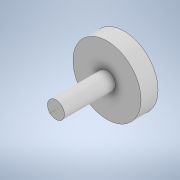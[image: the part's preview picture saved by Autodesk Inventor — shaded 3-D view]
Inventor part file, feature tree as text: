
AUTODESK INVENTOR PART (.ipt)
format: ipt  version: 2021.1 (Build 251245000, 245)  size: 105,984 bytes
history: native  units: in
note: dims shown in document units (in); Inventor stores cm internally (conversion verified against a paired STEP export)
features: extrude x3, sketch x3
ambient origin geometry x8: Origin, YZ Plane, XZ Plane, XY Plane, X Axis, Y Axis, Z Axis, Center Point
bodies: Solid1 (feature_tree)
feature tree (6):
  extrude  "Extrusion1"  Depth=0.25in TaperAngle=0.0deg
  extrude  "Extrusion2"  Depth=0.25in TaperAngle=0.0deg
  extrude  "Extrusion3"  [1 undecoded]
  sketch  "Sketch1"  dims[d0=1.0in d1=0.25in d2=0.0in]
  sketch  "Sketch2"  dims[d3=0.25in d4=0.25in d5=0.0in]
  sketch  "Sketch3"  dims[d6=0.5in d7=0.0in]
note: 1 required parameter value undecoded (feature->parameter linkage not recoverable at this tier; creation-order binding heuristic only, values carry confidence <= 0.55)
